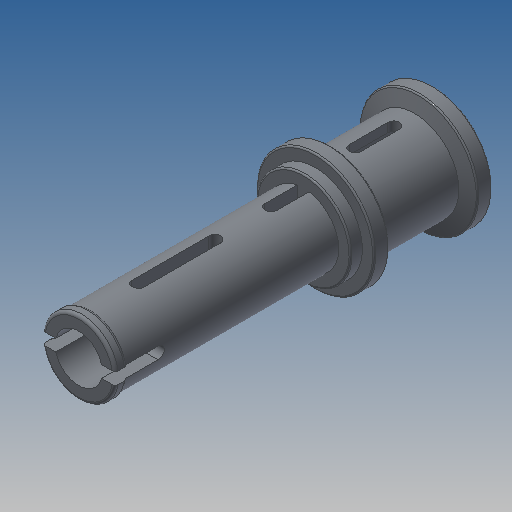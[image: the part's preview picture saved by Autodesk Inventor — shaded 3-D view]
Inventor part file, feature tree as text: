
AUTODESK INVENTOR PART (.ipt)
format: ipt  version: 2022.2 (Build 262287000, 287)  size: 338,944 bytes
history: native  units: mm (DEFAULTED — no unit token found)
features: sketch x3, extrude x3, revolve x1, fillet x1
ambient origin geometry x8: Origin, YZ Plane, XZ Plane, XY Plane, X Axis, Y Axis, Z Axis, Center Point
bodies: Solid2 (feature_tree)
feature tree (8):
  sketch  "Sketch1"  dims[d1=4.8mm d2=5.0mm d4=0.75mm]
  revolve  "Revolution1"  [1 undecoded]
  fillet  "Fillet1"  Radius=0.75mm
  extrude  "Extrusion1"  Depth=0.8mm
  extrude  "Extrusion2"  Depth=10.0mm
  extrude  "Extrusion3"  Depth=10.0mm
  sketch  "Sketch2"  dims[d6=16.0mm d7=0.8mm]
  sketch  "Sketch3"  dims[d8=6.4mm d9=0.8mm d14=0.8mm d16=6.0mm d17=0.8mm d18=4.0mm d19=8.0mm d20=90.0deg d21=10.0mm d22=0.0mm d25=10.0mm d26=0.0mm d27=0.2mm d28=0.1mm d29=0.0mm d30=8.0mm d32=4.8mm d33=1.0mm d35=15.0deg d36=0.6mm d37=3.4mm d38=3.4mm d41=0.8mm d42=4.8mm d43=1.6mm d44=10.0mm d45=0.0mm d46=3.2mm d47=3.4mm d48=0.0mm]
note: 1 required parameter value undecoded (feature->parameter linkage not recoverable at this tier; creation-order binding heuristic only, values carry confidence <= 0.55)
